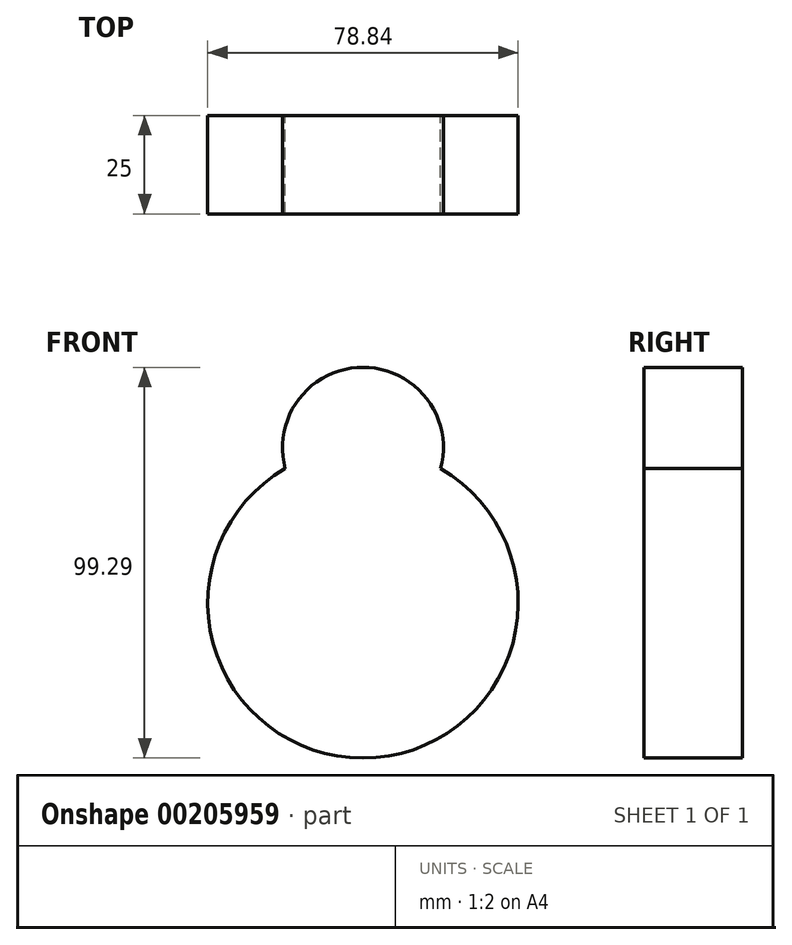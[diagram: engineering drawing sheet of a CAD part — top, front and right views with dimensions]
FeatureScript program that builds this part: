
annotation { "Feature Type Name" : "Feature", "Feature Type Description" : "" }
export const myFeature = defineFeature(function(context is Context, id is Id, definition is map)
    precondition{}
    {
        {
            var Q0;
            Q0=qCreatedBy(makeId("Front.planeOp"),FACE);
            var sketch = newSketch(context, id + "F0", { "sketchPlane" : qUnion([Q0])});
            skCircle(sketch, "E0", {"center": v(0, 3.46) * mm, "radius": 39.42 * mm});
            skCircle(sketch, "E1", {"center": v(0, 42.88) * mm, "radius": 20.45 * mm});
            skSolve(sketch);
        }
        {
            var Q0;
            {var subQ0=sQuery(id+"F0.wireOp",EDGE,"E1");var subQ1=sQuery(id+"F0.wireOp",EDGE,"E0");var subQ2=makeQuery(id+"F0.imprint","INTERSECT",VERTEX,{"disambiguationData":[OD(0.0)],"derivedFrom":[subQ1,subQ0]});Q0=makeQuery(id+"F0.imprint","IMPRINT",FACE,{"disambiguationData":[TD([[makeQuery(id+"F0.imprint","IMPRINT",EDGE,{"disambiguationData":[TD([[subQ2,1.0]])],"derivedFrom":subQ1}),-1.0]])]});}
            var Q1;
            {var subQ0=sQuery(id+"F0.wireOp",EDGE,"E1");var subQ1=sQuery(id+"F0.wireOp",EDGE,"E0");var subQ2=makeQuery(id+"F0.imprint","INTERSECT",VERTEX,{"disambiguationData":[OD(0.0)],"derivedFrom":[subQ1,subQ0]});Q1=makeQuery(id+"F0.imprint","IMPRINT",FACE,{"disambiguationData":[TD([[makeQuery(id+"F0.imprint","IMPRINT",EDGE,{"disambiguationData":[TD([[subQ2,1.0]])],"derivedFrom":subQ1}),1.0]])]});}
            var Q2;
            {var subQ0=sQuery(id+"F0.wireOp",EDGE,"E1");var subQ1=sQuery(id+"F0.wireOp",EDGE,"E0");var subQ2=makeQuery(id+"F0.imprint","INTERSECT",VERTEX,{"disambiguationData":[OD(0.0)],"derivedFrom":[subQ1,subQ0]});Q2=makeQuery(id+"F0.imprint","IMPRINT",FACE,{"disambiguationData":[TD([[makeQuery(id+"F0.imprint","IMPRINT",EDGE,{"disambiguationData":[TD([[subQ2,-1.0]])],"derivedFrom":subQ1}),1.0]])]});}
            extrude(context, id + "F1", {"entities" : qUnion([Q0, Q1, Q2]), "depth" : 25 * mm, "offsetDistance" : 25 * mm});
        }
    });
